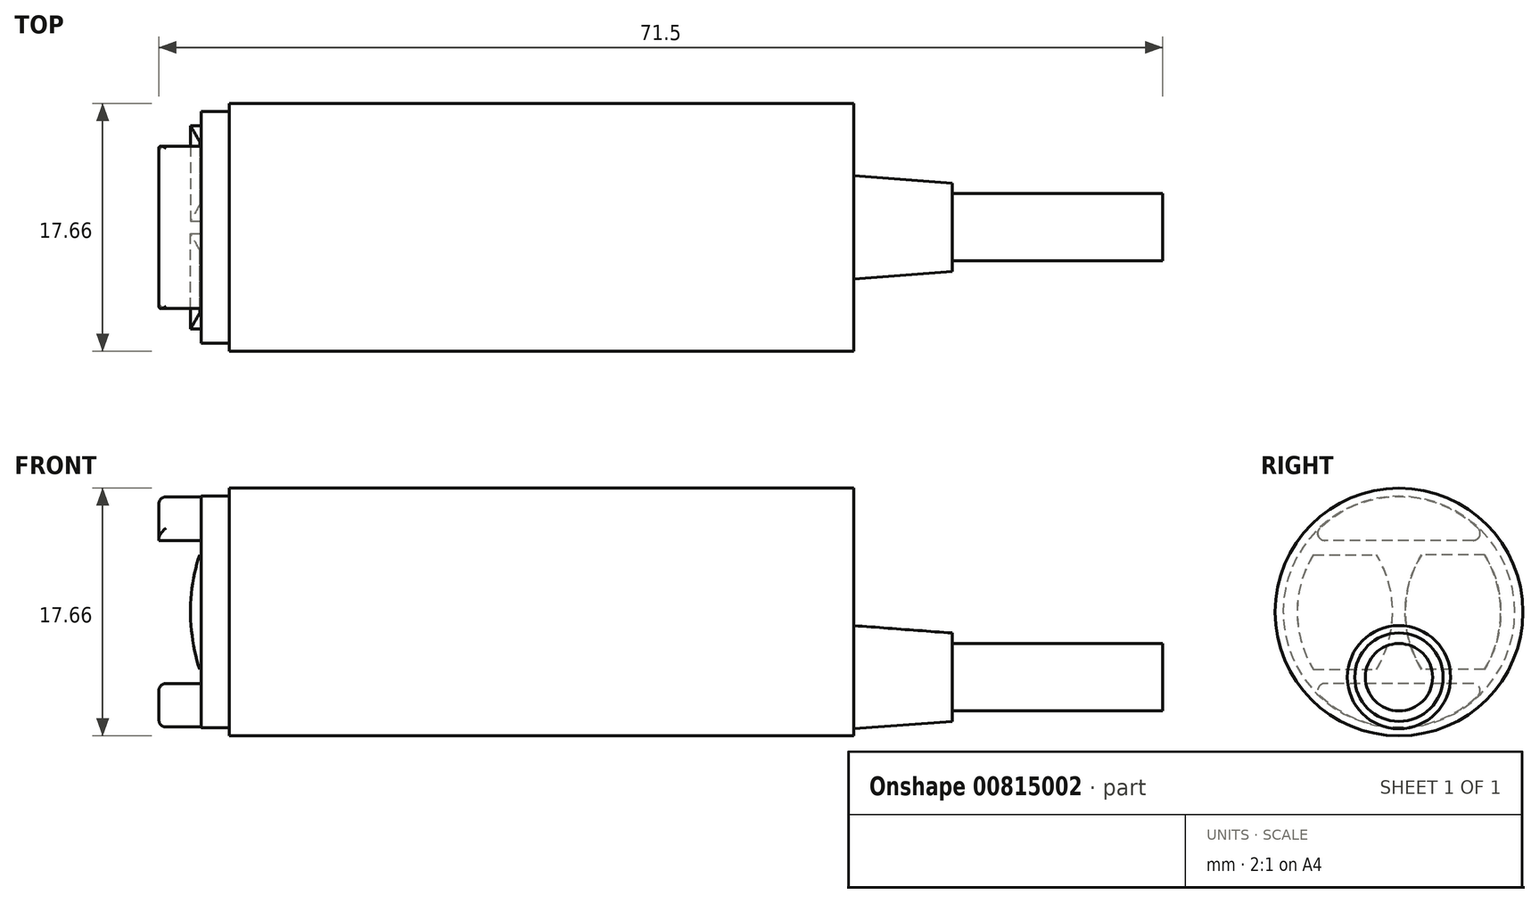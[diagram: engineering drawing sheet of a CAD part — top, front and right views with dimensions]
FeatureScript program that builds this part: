
annotation { "Feature Type Name" : "Feature", "Feature Type Description" : "" }
export const myFeature = defineFeature(function(context is Context, id is Id, definition is map)
    precondition{}
    {
        {
            var Q0;
            Q0=qCreatedBy(makeId("Front.planeOp"),FACE);
            var sketch = newSketch(context, id + "F0", { "sketchPlane" : qUnion([Q0])});
            skLineSegment(sketch, "E0", {"start": v(-49.5, 0) * mm, "end": v(-49.5, 8.2) * mm});
            skLineSegment(sketch, "E1", {"start": v(-49.5, 8.2) * mm, "end": v(-46.5, 8.2) * mm});
            skLineSegment(sketch, "E2", {"start": v(-46.5, 8.2) * mm, "end": v(-46.5, 8.25) * mm});
            skLineSegment(sketch, "E3", {"start": v(-46.5, 8.25) * mm, "end": v(-44.5, 8.25) * mm});
            skLineSegment(sketch, "E4", {"start": v(-44.5, 8.25) * mm, "end": v(-44.5, 8.82) * mm});
            skLineSegment(sketch, "E5", {"start": v(-44.5, 8.82) * mm, "end": v(0, 8.82) * mm});
            skLineSegment(sketch, "E6", {"start": v(0, 8.82) * mm, "end": v(0, 0) * mm});
            skLineSegment(sketch, "E7", {"start": v(0, 0) * mm, "end": v(-49.5, 0) * mm});
            skSolve(sketch);
        }
        {
            var Q0;
            Q0=makeQuery(id+"F0.imprint","IMPRINT",FACE,{"disambiguationData":[TD([[makeQuery(id+"F0.imprint","IMPRINT",EDGE,{"derivedFrom":sQuery(id+"F0.wireOp",EDGE,"E0")}),-1.0]])]});
            var Q1;
            Q1=sQuery(id+"F0.wireOp",EDGE,"E7");
            revolve(context, id + "F1", {"entities" : qUnion([Q0]), "axis" : qUnion([Q1]), "revolveType" : RevolveType.FULL});
        }
        {
            var Q0;
            Q0=qCreatedBy(makeId("Front.planeOp"),FACE);
            var sketch = newSketch(context, id + "F2", { "sketchPlane" : qUnion([Q0])});
            skLineSegment(sketch, "E8.bottom", {"start": v(-49.5, 5.1) * mm, "end": v(-46.5, 5.1) * mm});
            skLineSegment(sketch, "E8.top", {"start": v(-49.5, -5.1) * mm, "end": v(-46.5, -5.1) * mm});
            skLineSegment(sketch, "E8.left", {"start": v(-49.5, 5.1) * mm, "end": v(-49.5, -5.1) * mm});
            skLineSegment(sketch, "E8.right", {"start": v(-46.5, 5.1) * mm, "end": v(-46.5, -5.1) * mm});
            skSolve(sketch);
        }
        {
            var Q0;
            Q0=qSketchRegion(id+"F2",true);
            extrude(context, id + "F3", {"entities" : qUnion([Q0]), "operationType" : NewBodyOperationType.REMOVE, "endBound" : BoundingType.SYMMETRIC, "oppositeDirection" : true, "depth" : 25 * mm});
        }
        {
            var Q0;
            Q0=makeQuery(id+"F3.boolean.opBoolean","COPY",EDGE,{"derivedFrom":makeQuery(id+"F3.opExtrude","SWEPT_EDGE",EDGE,{"disambiguationData":[OSD([sQuery(id+"F2.wireOp",EDGE,"E8.bottom"),sQuery(id+"F2.wireOp",EDGE,"E8.left")])]})});
            var Q1;
            Q1=makeQuery(id+"F3.boolean.opBoolean","INTERSECT",EDGE,{"disambiguationData":[OD(0.0)],"derivedFrom":[makeQuery(id+"F1.opRevolve","SWEPT_FACE",FACE,{"disambiguationData":[OSD([sQuery(id+"F0.wireOp",EDGE,"E1")])]}),makeQuery(id+"F3.opExtrude","SWEPT_FACE",FACE,{"disambiguationData":[OSD([sQuery(id+"F2.wireOp",EDGE,"E8.bottom")])]})]});
            var Q2;
            {var subQ0=sQuery(id+"F0.wireOp",EDGE,"E0");var subQ1=sQuery(id+"F0.wireOp",EDGE,"E1");Q2=makeQuery(id+"F3.boolean.opBoolean","SPLIT",EDGE,{"disambiguationData":[TD([makeQuery(id+"F3.opExtrude","SWEPT_FACE",FACE,{"disambiguationData":[OSD([sQuery(id+"F2.wireOp",EDGE,"E8.bottom")])]})])],"derivedFrom":makeQuery(id+"F1.opRevolve","SWEPT_EDGE",EDGE,{"disambiguationData":[OSD([subQ0,subQ1])]})});}
            var Q3;
            Q3=makeQuery(id+"F3.boolean.opBoolean","INTERSECT",EDGE,{"disambiguationData":[OD(1.0)],"derivedFrom":[makeQuery(id+"F1.opRevolve","SWEPT_FACE",FACE,{"disambiguationData":[OSD([sQuery(id+"F0.wireOp",EDGE,"E1")])]}),makeQuery(id+"F3.opExtrude","SWEPT_FACE",FACE,{"disambiguationData":[OSD([sQuery(id+"F2.wireOp",EDGE,"E8.bottom")])]})]});
            var Q4;
            Q4=makeQuery(id+"F3.boolean.opBoolean","INTERSECT",EDGE,{"disambiguationData":[OD(1.0)],"derivedFrom":[makeQuery(id+"F1.opRevolve","SWEPT_FACE",FACE,{"disambiguationData":[OSD([sQuery(id+"F0.wireOp",EDGE,"E1")])]}),makeQuery(id+"F3.opExtrude","SWEPT_FACE",FACE,{"disambiguationData":[OSD([sQuery(id+"F2.wireOp",EDGE,"E8.top")])]})]});
            var Q5;
            Q5=makeQuery(id+"F3.boolean.opBoolean","INTERSECT",EDGE,{"disambiguationData":[OD(0.0)],"derivedFrom":[makeQuery(id+"F1.opRevolve","SWEPT_FACE",FACE,{"disambiguationData":[OSD([sQuery(id+"F0.wireOp",EDGE,"E1")])]}),makeQuery(id+"F3.opExtrude","SWEPT_FACE",FACE,{"disambiguationData":[OSD([sQuery(id+"F2.wireOp",EDGE,"E8.top")])]})]});
            var Q6;
            {var subQ0=sQuery(id+"F0.wireOp",EDGE,"E0");var subQ1=sQuery(id+"F0.wireOp",EDGE,"E1");Q6=makeQuery(id+"F3.boolean.opBoolean","SPLIT",EDGE,{"disambiguationData":[TD([makeQuery(id+"F3.opExtrude","SWEPT_FACE",FACE,{"disambiguationData":[OSD([sQuery(id+"F2.wireOp",EDGE,"E8.top")])]})])],"derivedFrom":makeQuery(id+"F1.opRevolve","SWEPT_EDGE",EDGE,{"disambiguationData":[OSD([subQ0,subQ1])]})});}
            var Q7;
            Q7=makeQuery(id+"F3.boolean.opBoolean","COPY",EDGE,{"derivedFrom":makeQuery(id+"F3.opExtrude","SWEPT_EDGE",EDGE,{"disambiguationData":[OSD([sQuery(id+"F2.wireOp",EDGE,"E8.top"),sQuery(id+"F2.wireOp",EDGE,"E8.left")])]})});
            fillet(context, id + "F4", {"entities" : qUnion([Q0, Q1, Q2, Q3, Q4, Q5, Q6, Q7]), "radius" : 0.5 * mm, "tangentPropagation" : true, "allowEdgeOverflow" : false});
        }
        {
            var Q0;
            Q0=qCreatedBy(makeId("Top.planeOp"),FACE);
            cPlane(context, id + "F5", {"entities" : qUnion([Q0]), "cplaneType" : CPlaneType.OFFSET, "offset" : 4.65 * mm, "oppositeDirection" : true, "width" : 150 * mm, "height" : 150 * mm});
        }
        {
            var Q0;
            Q0=qCreatedBy(id+"F5.planeOp",FACE);
            var sketch = newSketch(context, id + "F6", { "sketchPlane" : qUnion([Q0])});
            skLineSegment(sketch, "E9", {"start": v(0, -3.67) * mm, "end": v(7, -3.15) * mm});
            skLineSegment(sketch, "E10", {"start": v(7, -3.15) * mm, "end": v(7, 0) * mm});
            skLineSegment(sketch, "E11", {"start": v(0, 0) * mm, "end": v(7, 0) * mm});
            skLineSegment(sketch, "E12", {"start": v(0, -3.67) * mm, "end": v(0, 0) * mm});
            skSolve(sketch);
        }
        {
            var Q0;
            Q0=makeQuery(id+"F6.imprint","IMPRINT",FACE,{"disambiguationData":[TD([[makeQuery(id+"F6.imprint","IMPRINT",EDGE,{"derivedFrom":sQuery(id+"F6.wireOp",EDGE,"E9")}),1.0]])]});
            var Q1;
            Q1=sQuery(id+"F6.wireOp",EDGE,"E11");
            revolve(context, id + "F7", {"entities" : qUnion([Q0]), "axis" : qUnion([Q1]), "revolveType" : RevolveType.FULL});
        }
        {
            var Q0;
            Q0=qCreatedBy(id+"F5.planeOp",FACE);
            var sketch = newSketch(context, id + "F8", { "sketchPlane" : qUnion([Q0])});
            skLineSegment(sketch, "E13.bottom", {"start": v(7, 0) * mm, "end": v(22, 0) * mm});
            skLineSegment(sketch, "E13.top", {"start": v(7, 2.4) * mm, "end": v(22, 2.4) * mm});
            skLineSegment(sketch, "E13.left", {"start": v(7, 0) * mm, "end": v(7, 2.4) * mm});
            skLineSegment(sketch, "E13.right", {"start": v(22, 0) * mm, "end": v(22, 2.4) * mm});
            skSolve(sketch);
        }
        {
            var Q0;
            Q0=qSketchRegion(id+"F8",true);
            var Q1;
            Q1=sQuery(id+"F8.wireOp",EDGE,"E13.bottom");
            revolve(context, id + "F9", {"entities" : qUnion([Q0]), "axis" : qUnion([Q1]), "revolveType" : RevolveType.FULL});
        }
        {
            var Q0;
            Q0=makeQuery(id+"F3.boolean.opBoolean","MERGE",FACE,{"derivedFrom":[makeQuery(id+"F1.opRevolve","SWEPT_FACE",FACE,{"disambiguationData":[OSD([sQuery(id+"F0.wireOp",EDGE,"E2")])]}),makeQuery(id+"F3.opExtrude","SWEPT_FACE",FACE,{"disambiguationData":[OSD([sQuery(id+"F2.wireOp",EDGE,"E8.right")])]})]});
            var sketch = newSketch(context, id + "F10", { "sketchPlane" : qUnion([Q0])});
            skArc(sketch, "E14", {"start": v(-6.1, 4.08) * mm, "mid": v(-7.25, 0) * mm, "end": v(-6.1, -4.08) * mm});
            skArc(sketch, "E15", {"start": v(-1.6, -4.08) * mm, "mid": v(-0.45, 0) * mm, "end": v(-1.6, 4.08) * mm});
            skLineSegment(sketch, "E16", {"start": v(-6.1, -4.08) * mm, "end": v(-1.6, -4.08) * mm});
            skLineSegment(sketch, "E17.MirrorCS", {"start": v(-6.1, 4.08) * mm, "end": v(-1.6, 4.08) * mm});
            skLineSegment(sketch, "E18", {"start": v(-3.85, 4.08) * mm, "end": v(-3.85, -4.08) * mm, "construction": true});
            skSolve(sketch);
        }
        {
            var Q0;
            Q0=makeQuery(id+"F10.imprint","IMPRINT",FACE,{"disambiguationData":[TD([[makeQuery(id+"F10.imprint","IMPRINT",EDGE,{"derivedFrom":sQuery(id+"F10.wireOp",EDGE,"E14")}),1.0]])]});
            extrude(context, id + "F11", {"entities" : qUnion([Q0]), "depth" : 0.75 * mm});
        }
        {
            var Q0;
            Q0=qCreatedBy(makeId("Front.planeOp"),FACE);
            var sketch = newSketch(context, id + "F12", { "sketchPlane" : qUnion([Q0])});
            skArc(sketch, "E19", {"start": v(-46.6, 4.08) * mm, "mid": v(-47.25, 0) * mm, "end": v(-46.6, -4.08) * mm});
            skPoint(sketch, "E20", {"position": v(-46.6, 4.08) * mm});
            skLineSegment(sketch, "E21.0", {"start": v(-47.25, 4.08) * mm, "end": v(-46.5, 4.08) * mm});
            skPoint(sketch, "E22.0", {"position": v(-46.88, -4.08) * mm});
            skLineSegment(sketch, "E23", {"start": v(-47.25, 4.08) * mm, "end": v(-47.25, 0) * mm});
            skLineSegment(sketch, "E24", {"start": v(-47.25, 0) * mm, "end": v(-47.25, -4.08) * mm});
            skLineSegment(sketch, "E25", {"start": v(-47.25, -4.08) * mm, "end": v(-46.6, -4.08) * mm});
            skSolve(sketch);
        }
        {
            var Q0;
            Q0=qSketchRegion(id+"F12",true);
            extrude(context, id + "F13", {"entities" : qUnion([Q0]), "operationType" : NewBodyOperationType.REMOVE, "endBound" : BoundingType.THROUGH_ALL, "oppositeDirection" : true, "depth" : 25 * mm});
        }
        {
            var Q0;
            Q0=makeQuery(id+"F11.opExtrude","SWEPT_BODY",BODY,{"disambiguationData":[OSD([sQuery(id+"F10.wireOp",EDGE,"E14"),sQuery(id+"F10.wireOp",EDGE,"E15"),sQuery(id+"F10.wireOp",EDGE,"E16"),sQuery(id+"F10.wireOp",EDGE,"E17.MirrorCS")])]});
            var Q1;
            Q1=qCreatedBy(makeId("Front.planeOp"),FACE);
            mirror(context, id + "F14", {"operationType" : NewBodyOperationType.ADD, "entities" : qUnion([Q0]), "mirrorPlane" : qUnion([Q1])});
        }
    });
